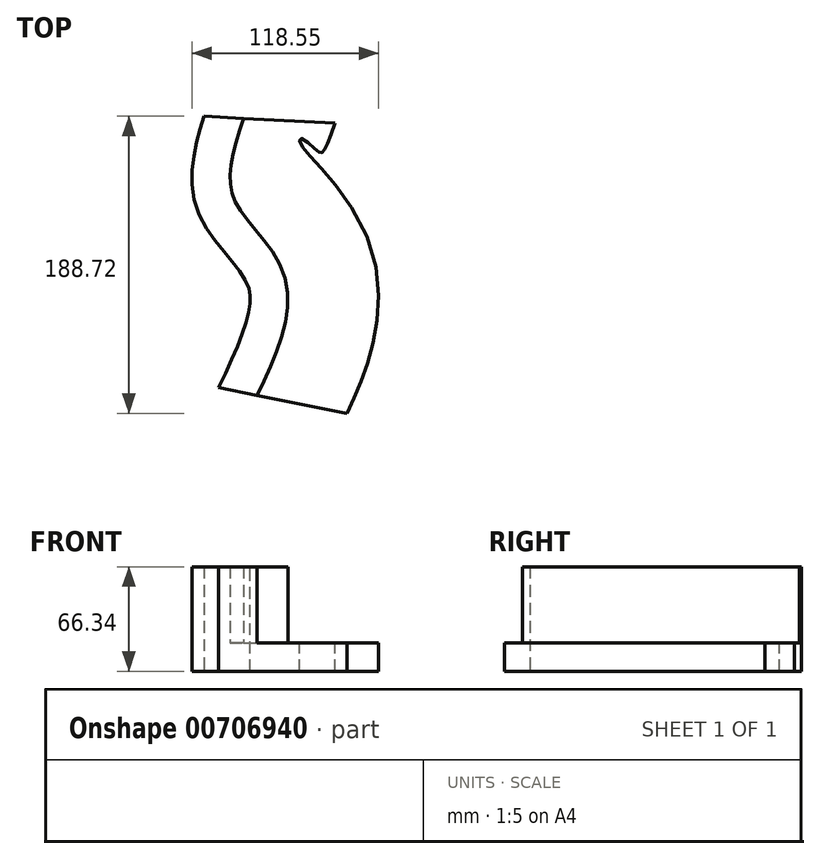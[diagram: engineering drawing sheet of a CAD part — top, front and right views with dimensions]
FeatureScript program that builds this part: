
annotation { "Feature Type Name" : "Feature", "Feature Type Description" : "" }
export const myFeature = defineFeature(function(context is Context, id is Id, definition is map)
    precondition{}
    {
        {
            var Q0;
            Q0=qCreatedBy(makeId("Front.planeOp"),FACE);
            var sketch = newSketch(context, id + "F0", { "sketchPlane" : qUnion([Q0])});
            skLineSegment(sketch, "E0.bottom", {"start": v(-41.74, 38.09) * mm, "end": v(-16.72, 38.09) * mm});
            skLineSegment(sketch, "E0.top", {"start": v(-41.74, -28.25) * mm, "end": v(-16.72, -28.25) * mm});
            skLineSegment(sketch, "E0.left", {"start": v(-41.74, 38.09) * mm, "end": v(-41.74, -28.25) * mm});
            skLineSegment(sketch, "E0.right", {"start": v(-16.72, 38.09) * mm, "end": v(-16.72, -28.25) * mm});
            skLineSegment(sketch, "E1.bottom", {"start": v(-16.72, -28.25) * mm, "end": v(41.46, -28.25) * mm});
            skLineSegment(sketch, "E1.top", {"start": v(-16.72, -10.26) * mm, "end": v(41.46, -10.26) * mm});
            skLineSegment(sketch, "E1.left", {"start": v(-16.72, -28.25) * mm, "end": v(-16.72, -10.26) * mm});
            skLineSegment(sketch, "E1.right", {"start": v(41.46, -28.25) * mm, "end": v(41.46, -10.26) * mm});
            skSolve(sketch);
        }
        {
            var Q0;
            Q0=qCreatedBy(makeId("Top.planeOp"),FACE);
            var sketch = newSketch(context, id + "F1", { "sketchPlane" : qUnion([Q0])});
            skFitSpline(sketch, "E2", {"points": [v(-21.2, 17.49) * mm, v(-26.47, -36.99) * mm, v(5.73, -86.2) * mm, v(-12.23, -157.09) * mm], "startDerivative": vector(-56.27, -182.48) * mm, "endDerivative": vector(-99.58, -209.77) * mm});
            skSolve(sketch);
        }
        {
            var Q0;
            Q0=makeQuery(id+"F0.imprint","IMPRINT",FACE,{"disambiguationData":[TD([[makeQuery(id+"F0.imprint","IMPRINT",EDGE,{"derivedFrom":sQuery(id+"F0.wireOp",EDGE,"E0.bottom")}),-1.0]])]});
            var Q1;
            Q1=makeQuery(id+"F0.imprint","IMPRINT",FACE,{"disambiguationData":[TD([[makeQuery(id+"F0.imprint","IMPRINT",EDGE,{"derivedFrom":sQuery(id+"F0.wireOp",EDGE,"E1.bottom")}),1.0]])]});
            var Q2;
            Q2=sQuery(id+"F1.wireOp",EDGE,"E2");
            sweep(context, id + "F2", {"profiles" : qUnion([Q0, Q1]), "path" : qUnion([Q2])});
        }
    });
